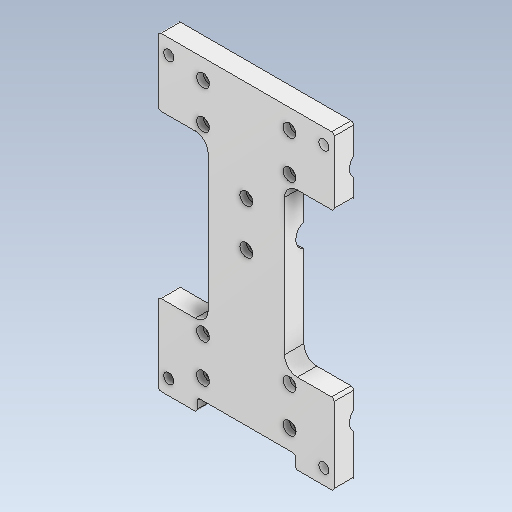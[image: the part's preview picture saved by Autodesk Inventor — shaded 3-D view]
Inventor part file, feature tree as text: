
AUTODESK INVENTOR PART (.ipt)
format: ipt  version: 2020 (Build 240168000, 168)  size: 274,944 bytes
history: native  units: mm
features: other x7, sketch x5, extrude x4, mirror x3, hole x3, fillet x2, reference x2, projected_geometry x1
ambient origin geometry x8: Origin, YZ Plane, XZ Plane, XY Plane, X Axis, Y Axis, Z Axis, Center Point
bodies: Solid1 (feature_tree)
feature tree (27):
  extrude  "Extrusion1"  Depth=136.0mm
  extrude  "Extrusion3"  Depth=19.5mm
  extrude  "Extrusion2"  TaperAngle=0.0deg  [1 undecoded]
  extrude  "Extrusion4"  Depth=8.0mm
  mirror  "Mirror1"
  hole  "Hole2"  [1 undecoded]
  hole  "Hole1"  [1 undecoded]
  mirror  "Mirror2"
  mirror  "Mirror3"
  fillet  "Fillet2"  Radius=29.0mm
  fillet  "Fillet3"  Radius=15.0mm
  hole  "Hole4"  [1 undecoded]
  sketch  "Sketch1"  dims[d0=230.0mm d1=136.0mm]
  sketch  "Sketch4"  dims[d2=15.0mm d3=0.0mm d6=19.5mm]
  projected_geometry  "Projected Loop1"
  sketch  "Sketch5"  dims[d7=30.0mm d8=0.0mm d9=0.0mm]
  sketch  "Sketch6"  dims[d10=11.75mm d11=8.0mm]
  reference  "Reference9"
  sketch  "Sketch8"  dims[d12=8.0mm d14=1.75mm d15=0.0mm d16=0.0mm d18=29.0mm d19=15.0mm d20=15.0mm d21=15.0mm d22=0.0mm d23=0.0mm d29=5.5mm d30=6.0mm d31=10.0mm d32=5.0mm d33=90.0deg d34=8.0mm d35=20.594885mm d37=5.5mm d39=34.5mm d40=77.75mm d41=5.5mm d42=6.0mm d43=10.0mm d44=5.0mm d45=90.0deg d46=8.0mm d47=20.594885mm d49=10.0mm d50=30.0mm d51=6.5mm d53=19.5mm d54=40.0mm d55=20.0mm d56=3.5mm d57=34.5mm d58=15.232779mm d59=29.534442mm d60=8.0mm d68=2.0mm d69=10.0mm d70=2.459mm d71=6.0mm d72=4.0mm d73=2.0mm d74=90.0deg d75=8.8mm d76=20.594885mm]
  reference  "Reference14"
  other  "<path> 2.1 Aracet.iam"
  other  "I.A.B 2.1 Aracet.iam"
  other  "0008-10-10 Injectomat Standard.iam:2"
  other  "0008-10-002 Corp_Injectomat1.ipt:10"
  parser-record x1  (decoder bookkeeping rows leaked as tree rows — omitted from the tree; the rows remain in map.json)
  other  "0008-10-02 X Axis.iam"
  other  "0008-20-1003 Switch:1"
note: 4 required parameter values undecoded (feature->parameter linkage not recoverable at this tier; creation-order binding heuristic only, values carry confidence <= 0.55)
note: 2 file-system paths scrubbed to <path> (originals preserved in map.json)
